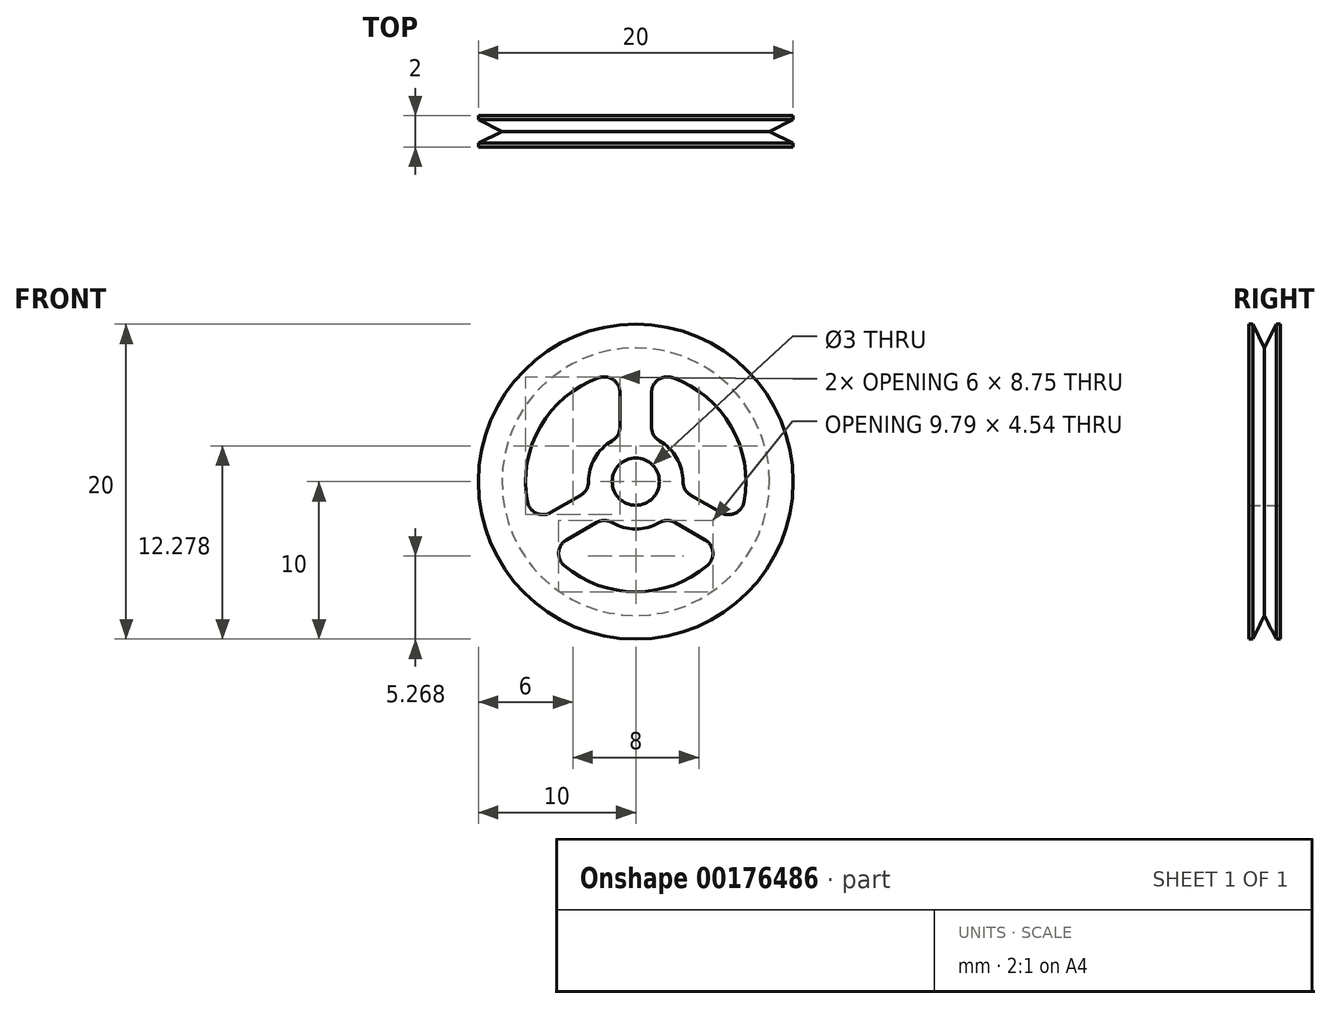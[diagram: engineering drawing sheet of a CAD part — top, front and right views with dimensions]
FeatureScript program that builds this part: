
annotation { "Feature Type Name" : "Feature", "Feature Type Description" : "" }
export const myFeature = defineFeature(function(context is Context, id is Id, definition is map)
    precondition{}
    {
        {
            var Q0;
            Q0=qCreatedBy(makeId("Front.planeOp"),FACE);
            var sketch = newSketch(context, id + "F0", { "sketchPlane" : qUnion([Q0])});
            skCircle(sketch, "E0", {"center": v(0, 0) * mm, "radius": 10 * mm});
            skArc(sketch, "E1.0", {"start": v(-2.33, 6.6) * mm, "mid": v(-6.06, 3.5) * mm, "end": v(-6.88, -1.28) * mm});
            skArc(sketch, "E2", {"start": v(-1.5, 2.6) * mm, "mid": v(-2.6, 1.5) * mm, "end": v(-3, 0) * mm});
            skCircle(sketch, "E3", {"center": v(0, 0) * mm, "radius": 1.5 * mm});
            skLineSegment(sketch, "E4.0", {"start": v(-1, 5.66) * mm, "end": v(-1, 3.46) * mm});
            skLineSegment(sketch, "E5.0", {"start": v(1, 5.66) * mm, "end": v(1, 3.46) * mm});
            skLineSegment(sketch, "E6.1.0", {"start": v(-4.4, -3.7) * mm, "end": v(-2.5, -2.6) * mm});
            skLineSegment(sketch, "E6.1.1", {"start": v(-5.4, -1.96) * mm, "end": v(-3.5, -0.87) * mm});
            skLineSegment(sketch, "E6.2.0", {"start": v(5.4, -1.96) * mm, "end": v(3.5, -0.87) * mm});
            skLineSegment(sketch, "E6.2.1", {"start": v(4.4, -3.7) * mm, "end": v(2.5, -2.6) * mm});
            skArc(sketch, "E7.trimOffspring", {"start": v(3, 0) * mm, "mid": v(2.6, 1.5) * mm, "end": v(1.5, 2.6) * mm});
            skArc(sketch, "E8.trimOffspring", {"start": v(-1.5, -2.6) * mm, "mid": v(0, -3) * mm, "end": v(1.5, -2.6) * mm});
            skArc(sketch, "E9.trimOffspring", {"start": v(-4.55, -5.32) * mm, "mid": v(0, -7) * mm, "end": v(4.55, -5.32) * mm});
            skArc(sketch, "E10.trimOffspring", {"start": v(6.88, -1.28) * mm, "mid": v(6.06, 3.5) * mm, "end": v(2.33, 6.6) * mm});
            skPoint(sketch, "E11.newPointB", {"position": v(-1, 10) * mm});
            skArc(sketch, "E11.filletArc", {"start": v(-1, 5.66) * mm, "mid": v(-1.42, 6.47) * mm, "end": v(-2.33, 6.6) * mm});
            skPoint(sketch, "E12.visualSharp", {"position": v(-1, 2.83) * mm});
            skArc(sketch, "E12.filletArc", {"start": v(-1.5, 2.6) * mm, "mid": v(-1.13, 2.96) * mm, "end": v(-1, 3.46) * mm});
            skPoint(sketch, "E13.visualSharp", {"position": v(-2.95, -0.55) * mm});
            skArc(sketch, "E13.filletArc", {"start": v(-3.5, -0.87) * mm, "mid": v(-3.13, -0.5) * mm, "end": v(-3, 0) * mm});
            skPoint(sketch, "E14.newPointA", {"position": v(-9.16, -4.13) * mm});
            skArc(sketch, "E14.filletArc", {"start": v(-6.88, -1.28) * mm, "mid": v(-6.32, -2) * mm, "end": v(-5.4, -1.96) * mm});
            skPoint(sketch, "E15.newPointB", {"position": v(-8.16, -5.87) * mm});
            skArc(sketch, "E15.filletArc", {"start": v(-4.4, -3.7) * mm, "mid": v(-4.9, -4.47) * mm, "end": v(-4.55, -5.32) * mm});
            skPoint(sketch, "E16.visualSharp", {"position": v(-1.95, -2.28) * mm});
            skArc(sketch, "E16.filletArc", {"start": v(-1.5, -2.6) * mm, "mid": v(-2, -2.46) * mm, "end": v(-2.5, -2.6) * mm});
            skPoint(sketch, "E17.visualSharp", {"position": v(1.95, -2.28) * mm});
            skArc(sketch, "E17.filletArc", {"start": v(2.5, -2.6) * mm, "mid": v(2, -2.46) * mm, "end": v(1.5, -2.6) * mm});
            skPoint(sketch, "E18.newPointB", {"position": v(8.16, -5.87) * mm});
            skArc(sketch, "E18.filletArc", {"start": v(4.55, -5.32) * mm, "mid": v(4.9, -4.47) * mm, "end": v(4.4, -3.7) * mm});
            skPoint(sketch, "E19.newPointA", {"position": v(9.16, -4.13) * mm});
            skArc(sketch, "E19.filletArc", {"start": v(5.4, -1.96) * mm, "mid": v(6.32, -2) * mm, "end": v(6.88, -1.28) * mm});
            skPoint(sketch, "E20.visualSharp", {"position": v(2.95, -0.55) * mm});
            skArc(sketch, "E20.filletArc", {"start": v(3, 0) * mm, "mid": v(3.13, -0.5) * mm, "end": v(3.5, -0.87) * mm});
            skPoint(sketch, "E21.visualSharp", {"position": v(1, 2.83) * mm});
            skArc(sketch, "E21.filletArc", {"start": v(1, 3.46) * mm, "mid": v(1.13, 2.96) * mm, "end": v(1.5, 2.6) * mm});
            skPoint(sketch, "E22.newPointA", {"position": v(1, 10) * mm});
            skArc(sketch, "E22.filletArc", {"start": v(2.33, 6.6) * mm, "mid": v(1.42, 6.47) * mm, "end": v(1, 5.66) * mm});
            skSolve(sketch);
        }
        {
            var Q0;
            Q0=makeQuery(id+"F0.imprint","IMPRINT",FACE,{"disambiguationData":[TD([[makeQuery(id+"F0.imprint","IMPRINT",EDGE,{"derivedFrom":sQuery(id+"F0.wireOp",EDGE,"E0")}),1.0]])]});
            extrude(context, id + "F1", {"entities" : qUnion([Q0]), "endBound" : BoundingType.SYMMETRIC, "depth" : 2 * mm});
        }
        {
            var Q0;
            Q0=qCreatedBy(makeId("Right.planeOp"),FACE);
            var sketch = newSketch(context, id + "F2", { "sketchPlane" : qUnion([Q0])});
            skLineSegment(sketch, "E23", {"start": v(0, 8.5) * mm, "end": v(0, 10) * mm});
            skLineSegment(sketch, "E24", {"start": v(0, 10) * mm, "end": v(0.75, 10) * mm});
            skLineSegment(sketch, "E25", {"start": v(0.75, 10) * mm, "end": v(0, 8.5) * mm});
            skLineSegment(sketch, "E26.MirrorCS", {"start": v(-0.75, 10) * mm, "end": v(0, 8.5) * mm});
            skLineSegment(sketch, "E27.MirrorCS", {"start": v(0, 10) * mm, "end": v(-0.75, 10) * mm});
            skLineSegment(sketch, "E28", {"start": v(4.44, 0) * mm, "end": v(-6, 0) * mm, "construction": true});
            skSolve(sketch);
        }
        {
            var Q0;
            Q0=qSketchRegion(id+"F2",true);
            var Q1;
            Q1=sQuery(id+"F2.wireOp",EDGE,"E28");
            revolve(context, id + "F3", {"operationType" : NewBodyOperationType.REMOVE, "entities" : qUnion([Q0]), "axis" : qUnion([Q1]), "revolveType" : RevolveType.FULL, "oppositeDirection" : true});
        }
    });
